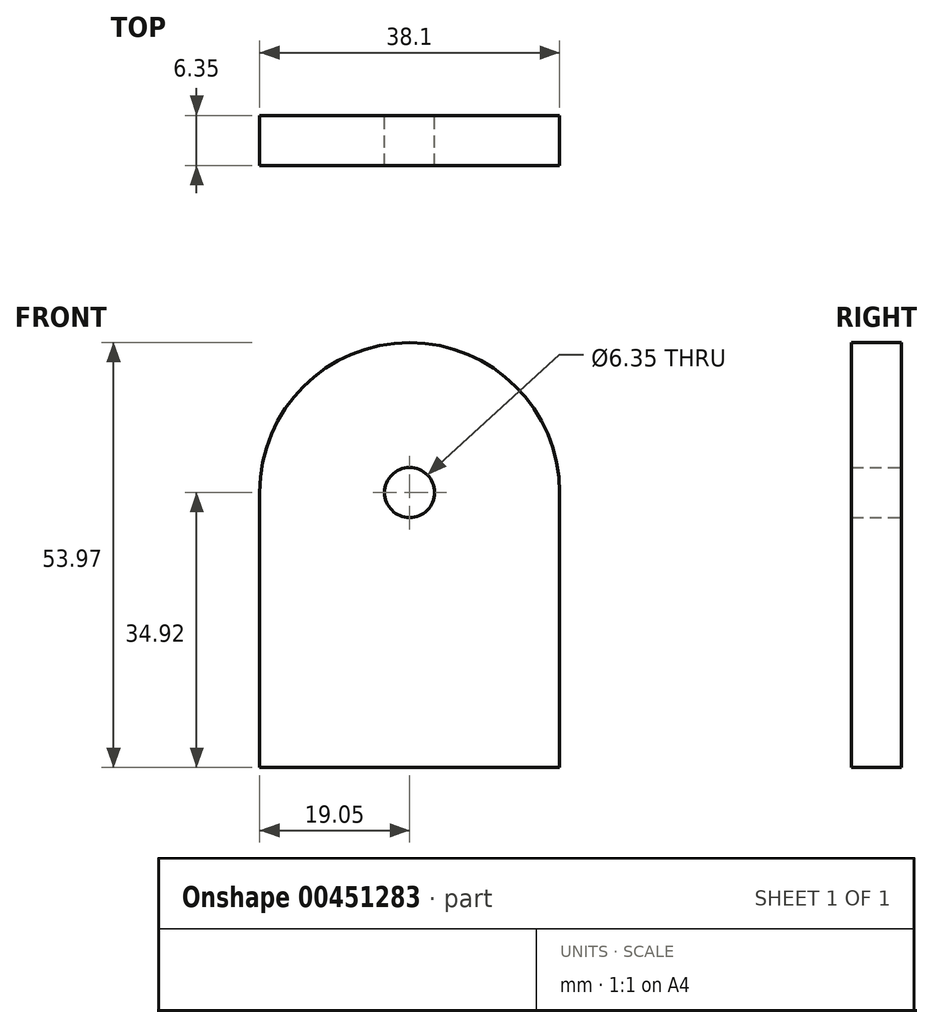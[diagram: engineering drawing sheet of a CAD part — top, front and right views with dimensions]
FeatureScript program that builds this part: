
annotation { "Feature Type Name" : "Feature", "Feature Type Description" : "" }
export const myFeature = defineFeature(function(context is Context, id is Id, definition is map)
    precondition{}
    {
        {
            var Q0;
            Q0=qCreatedBy(makeId("Front.planeOp"),FACE);
            var sketch = newSketch(context, id + "F0", { "sketchPlane" : qUnion([Q0])});
            skCircle(sketch, "E0", {"center": v(0, 0) * mm, "radius": 3.18 * mm});
            skArc(sketch, "E1", {"start": v(19.05, 0) * mm, "mid": v(13.47, 13.47) * mm, "end": v(0, 19.05) * mm});
            skLineSegment(sketch, "E2", {"start": v(0, -34.92) * mm, "end": v(19.05, -34.92) * mm});
            skLineSegment(sketch, "E3", {"start": v(0, 49.46) * mm, "end": v(0, -57.92) * mm, "construction": true});
            skLineSegment(sketch, "E4", {"start": v(19.05, 0) * mm, "end": v(19.05, -34.92) * mm});
            skLineSegment(sketch, "E5.MirrorCS", {"start": v(0, -34.92) * mm, "end": v(-19.05, -34.92) * mm});
            skLineSegment(sketch, "E6.MirrorCS", {"start": v(-19.05, 0) * mm, "end": v(-19.05, -34.93) * mm});
            skArc(sketch, "E7.MirrorCS", {"start": v(-19.05, 0) * mm, "mid": v(-13.47, 13.47) * mm, "end": v(0, 19.05) * mm});
            skSolve(sketch);
        }
        {
            var Q0;
            Q0 = qSketchRegion(id + "F0", true);
            extrude(context, id + "F1", {"entities" : qUnion([Q0]), "flatOperationType" : FlatOperationType.REMOVE, "offsetDistance" : 25.4 * mm, "depth" : 6.35 * mm, "domain" : OperationDomain.MODEL});
        }
    });
